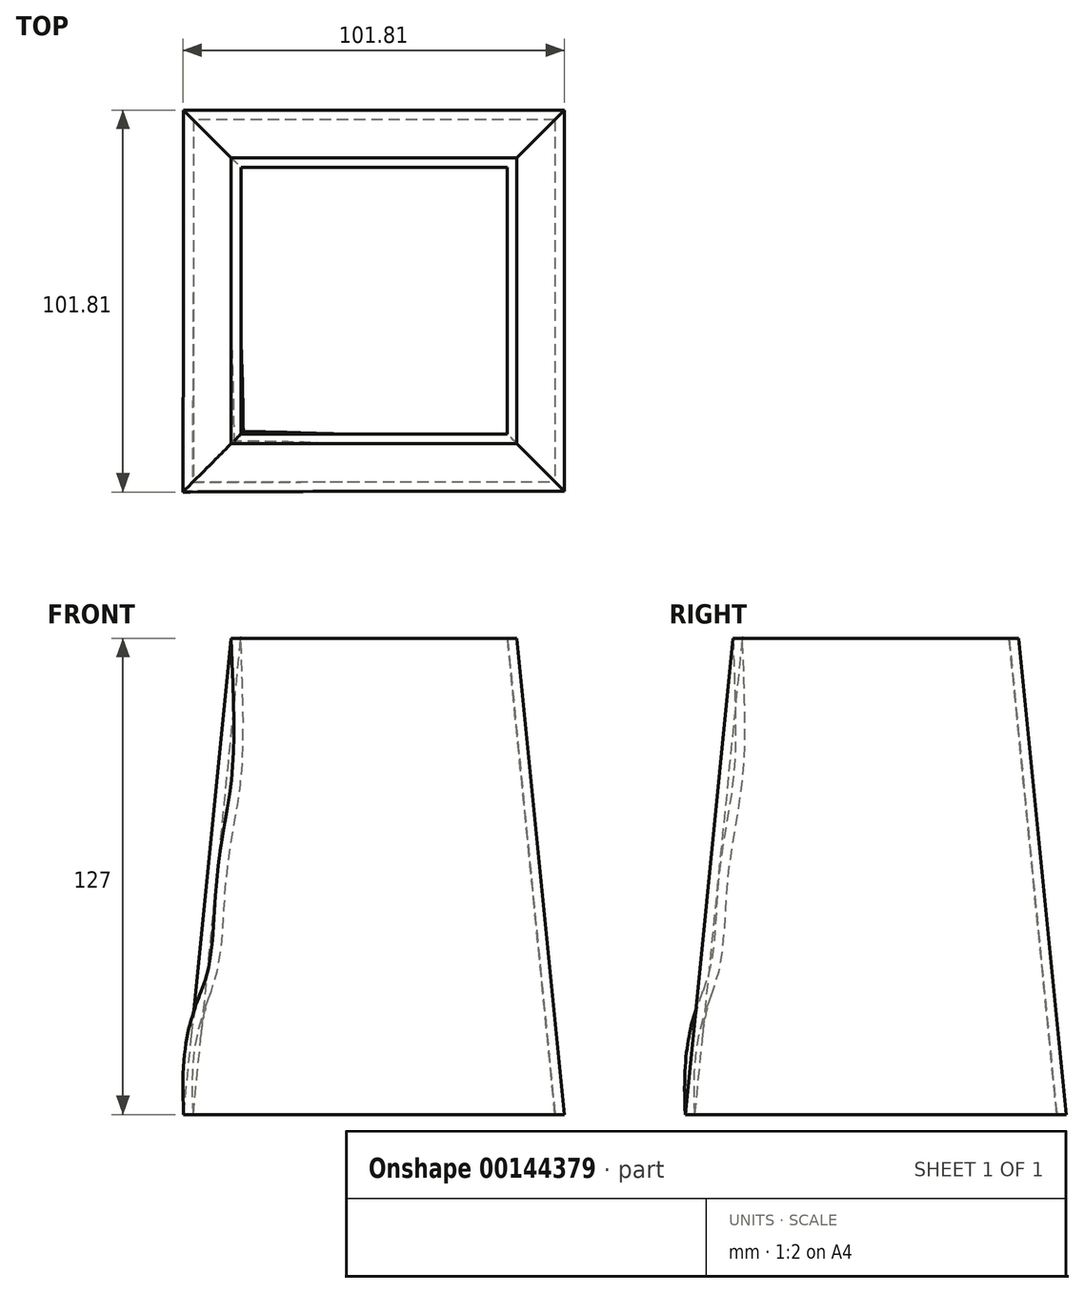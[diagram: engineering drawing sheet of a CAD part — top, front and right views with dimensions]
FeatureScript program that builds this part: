
annotation { "Feature Type Name" : "Feature", "Feature Type Description" : "" }
export const myFeature = defineFeature(function(context is Context, id is Id, definition is map)
    precondition{}
    {
        {
            var Q0;
            Q0=qCreatedBy(makeId("Top.planeOp"),FACE);
            cPlane(context, id + "F0", {"entities" : qUnion([Q0]), "cplaneType" : CPlaneType.OFFSET, "offset" : 127 * mm, "width" : 152.4 * mm, "height" : 152.4 * mm});
        }
        {
            var Q0;
            Q0=qCreatedBy(makeId("Top.planeOp"),FACE);
            var sketch = newSketch(context, id + "F1", { "sketchPlane" : qUnion([Q0])});
            skLineSegment(sketch, "E0.bottom", {"start": v(50.8, 50.8) * mm, "end": v(-50.8, 50.8) * mm});
            skLineSegment(sketch, "E0.top", {"start": v(50.8, -50.8) * mm, "end": v(-50.8, -50.8) * mm});
            skLineSegment(sketch, "E0.left", {"start": v(50.8, 50.8) * mm, "end": v(50.8, -50.8) * mm});
            skLineSegment(sketch, "E0.right", {"start": v(-50.8, 50.8) * mm, "end": v(-50.8, -50.8) * mm});
            skPoint(sketch, "E0.middle", {"position": v(0, 0) * mm});
            skSolve(sketch);
        }
        {
            var Q0;
            Q0=qCreatedBy(id+"F0.planeOp",FACE);
            var sketch = newSketch(context, id + "F2", { "sketchPlane" : qUnion([Q0])});
            skLineSegment(sketch, "E1.bottom", {"start": v(38.1, 38.1) * mm, "end": v(-38.1, 38.1) * mm});
            skLineSegment(sketch, "E1.top", {"start": v(38.1, -38.1) * mm, "end": v(-38.1, -38.1) * mm});
            skLineSegment(sketch, "E1.left", {"start": v(38.1, 38.1) * mm, "end": v(38.1, -38.1) * mm});
            skLineSegment(sketch, "E1.right", {"start": v(-38.1, 38.1) * mm, "end": v(-38.1, -38.1) * mm});
            skPoint(sketch, "E1.middle", {"position": v(0, 0) * mm});
            skSolve(sketch);
        }
        {
            var Q0;
            Q0=qCreatedBy(makeId("Top.planeOp"),FACE);
            cPlane(context, id + "F3", {"entities" : qUnion([Q0]), "cplaneType" : CPlaneType.OFFSET, "offset" : 88.9 * mm, "width" : 152.4 * mm, "height" : 152.4 * mm});
        }
        {
            var Q0;
            Q0=qCreatedBy(makeId("Top.planeOp"),FACE);
            cPlane(context, id + "F4", {"entities" : qUnion([Q0]), "cplaneType" : CPlaneType.OFFSET, "offset" : 63.5 * mm, "width" : 152.4 * mm, "height" : 152.4 * mm});
        }
        {
            var Q0;
            Q0=qCreatedBy(makeId("Top.planeOp"),FACE);
            cPlane(context, id + "F5", {"entities" : qUnion([Q0]), "cplaneType" : CPlaneType.OFFSET, "offset" : 38.1 * mm, "width" : 152.4 * mm, "height" : 152.4 * mm});
        }
        {
            var Q0;
            Q0=qCreatedBy(id+"F5.planeOp",FACE);
            var sketch = newSketch(context, id + "F6", { "sketchPlane" : qUnion([Q0])});
            skLineSegment(sketch, "E2.bottom", {"start": v(44.45, 44.45) * mm, "end": v(-44.45, 44.45) * mm});
            skLineSegment(sketch, "E2.top", {"start": v(44.45, -44.45) * mm, "end": v(-44.45, -44.45) * mm});
            skLineSegment(sketch, "E2.left", {"start": v(44.45, 44.45) * mm, "end": v(44.45, -44.45) * mm});
            skLineSegment(sketch, "E2.right", {"start": v(-44.45, 44.45) * mm, "end": v(-44.45, -44.45) * mm});
            skPoint(sketch, "E2.middle", {"position": v(0, 0) * mm});
            skSolve(sketch);
        }
        {
            var Q0;
            Q0=qCreatedBy(id+"F4.planeOp",FACE);
            var sketch = newSketch(context, id + "F7", { "sketchPlane" : qUnion([Q0])});
            skLineSegment(sketch, "E3.bottom", {"start": v(41.9, 41.91) * mm, "end": v(-41.91, 41.91) * mm});
            skLineSegment(sketch, "E3.top", {"start": v(41.91, -41.91) * mm, "end": v(-41.9, -41.91) * mm});
            skLineSegment(sketch, "E3.left", {"start": v(41.9, 41.91) * mm, "end": v(41.91, -41.91) * mm});
            skLineSegment(sketch, "E3.right", {"start": v(-41.91, 41.91) * mm, "end": v(-41.9, -41.91) * mm});
            skPoint(sketch, "E3.middle", {"position": v(0, 0) * mm});
            skSolve(sketch);
        }
        {
            var Q0;
            Q0=qCreatedBy(id+"F3.planeOp",FACE);
            var sketch = newSketch(context, id + "F8", { "sketchPlane" : qUnion([Q0])});
            skLineSegment(sketch, "E4.bottom", {"start": v(38.1, 38.1) * mm, "end": v(-38.1, 38.1) * mm});
            skLineSegment(sketch, "E4.top", {"start": v(38.1, -38.1) * mm, "end": v(-38.1, -38.1) * mm});
            skLineSegment(sketch, "E4.left", {"start": v(38.1, 38.1) * mm, "end": v(38.1, -38.1) * mm});
            skLineSegment(sketch, "E4.right", {"start": v(-38.1, 38.1) * mm, "end": v(-38.1, -38.1) * mm});
            skPoint(sketch, "E4.middle", {"position": v(0, 0) * mm});
            skSolve(sketch);
        }
        {
            var Q0;
            Q0=sQuery(id+"F2.wireOp",VERTEX,"E1.top.end");
            var Q1;
            Q1=sQuery(id+"F2.wireOp",VERTEX,"E1.left.start");
            var Q2;
            Q2=sQuery(id+"F1.wireOp",VERTEX,"E0.bottom.start");
            cPlane(context, id + "F9", {"entities" : qUnion([Q0, Q1, Q2]), "cplaneType" : CPlaneType.THREE_POINT, "offset" : 25.4 * mm, "width" : 152.4 * mm, "height" : 152.4 * mm});
        }
        {
            var Q0;
            Q0=qCreatedBy(id+"F9.planeOp",FACE);
            var sketch = newSketch(context, id + "F10", { "sketchPlane" : qUnion([Q0])});
            skFitSpline(sketch, "E5", {"points": [v(-53.88, 127) * mm, v(-53.88, 88.9) * mm, v(-59.27, 63.5) * mm, v(-62.86, 38.1) * mm, v(-71.84, 0) * mm], "startDerivative": vector(9.67, -197.74) * mm, "endDerivative": vector(20.34, -256.79) * mm});
            skSolve(sketch);
        }
        {
            var Q0;
            Q0=qCreatedBy(makeId("Right.planeOp"),FACE);
            var sketch = newSketch(context, id + "F11", { "sketchPlane" : qUnion([Q0])});
            skLineSegment(sketch, "E6", {"start": v(0, 0) * mm, "end": v(0, 99.92) * mm});
            skSolve(sketch);
        }
        {
            var Q0;
            Q0=makeQuery(id+"F1.imprint","IMPRINT",FACE,{"disambiguationData":[TD([[makeQuery(id+"F1.imprint","IMPRINT",EDGE,{"derivedFrom":sQuery(id+"F1.wireOp",EDGE,"E0.bottom")}),1.0]])]});
            var Q1;
            Q1=makeQuery(id+"F2.imprint","IMPRINT",FACE,{"disambiguationData":[TD([[makeQuery(id+"F2.imprint","IMPRINT",EDGE,{"derivedFrom":sQuery(id+"F2.wireOp",EDGE,"E1.bottom")}),1.0]])]});
            var Q2;
            Q2=sQuery(id+"F10.wireOp",EDGE,"E5");
            var Q3;
            Q3=sQuery(id+"FsYO0GiC6GIHdhr_0.1.F10.wireOp",EDGE,"E5");
            var Q4;
            Q4=sQuery(id+"FsYO0GiC6GIHdhr_0.2.F10.wireOp",EDGE,"E5");
            var Q5;
            Q5=sQuery(id+"FsYO0GiC6GIHdhr_0.3.F10.wireOp",EDGE,"E5");
            loft(context, id + "F12", {"addGuides" : true, "sheetProfilesArray" : [{ "sheetProfileEntities" : qUnion([Q0]) }, { "sheetProfileEntities" : qUnion([Q1]) }], "guidesArray" : [{ "guideEntities" : qUnion([Q2]), "guideDerivativeType" : LoftGuideDerivativeType.DEFAULT, "guideDerivativeMagnitude" : 1 }, { "guideEntities" : qUnion([Q3]), "guideDerivativeType" : LoftGuideDerivativeType.DEFAULT, "guideDerivativeMagnitude" : 1 }, { "guideEntities" : qUnion([Q4]), "guideDerivativeType" : LoftGuideDerivativeType.DEFAULT, "guideDerivativeMagnitude" : 1 }, { "guideEntities" : qUnion([Q5]), "guideDerivativeType" : LoftGuideDerivativeType.DEFAULT, "guideDerivativeMagnitude" : 1 }]});
        }
        {
            var Q0;
            Q0=makeQuery(id+"F12.opLoft","CAP_FACE",FACE,{"disambiguationData":[OSD([makeQuery(id+"F2.imprint","IMPRINT",FACE,{"disambiguationData":[TD([[makeQuery(id+"F2.imprint","IMPRINT",EDGE,{"derivedFrom":sQuery(id+"F2.wireOp",EDGE,"E1.bottom")}),1.0]])]})])],"isStart":true});
            var Q1;
            Q1=makeQuery(id+"F12.opLoft","CAP_FACE",FACE,{"disambiguationData":[OSD([makeQuery(id+"F1.imprint","IMPRINT",FACE,{"disambiguationData":[TD([[makeQuery(id+"F1.imprint","IMPRINT",EDGE,{"derivedFrom":sQuery(id+"F1.wireOp",EDGE,"E0.bottom")}),1.0]])]})])],"isStart":true});
            shell(context, id + "F13", {"entities" : qUnion([Q0, Q1]), "thickness" : 2.54 * mm});
        }
    });
